# Revit family: vl-100s3_50Hz
name_source: partatom
category: 機械設備
units: mm (PartAtom-declared; Revit-internal decimal feet)

## family parameters
OmniClass タイトル = Centrifugal Fans
OmniClass 番号 = 23.75.35.17.27
パーツ タイプ = 標準
ロード時にボイドで切り取り = いいえ
丸型コネクタ寸法 = 直径を使用
作業面ベース = いいえ
共有 = いいえ
常に垂直 = はい
部屋計算ポイント = いいえ

## types (1)
- VL-100S3
    Clearance Back = 0  [stored 0 ft]
    Clearance Bottom = 100  [stored 0.328084 ft]
    Clearance Front = 500  [stored 1.64042 ft]
    Clearance Left = 50
    Clearance Right = 50
    Clearance Top = 120
    D1 = 206  [stored 0.675853 ft]
    Depth = 156  [stored 0.511811 ft]
    H1 = 289  [stored 0.948163 ft]
    H2 = 115  [stored 0.377297 ft]
    H3 = 137  [stored 0.449475 ft]
    Height = 235
    IfcExportAs = IfcFanType
    IfcExportType = CENTRIFUGALBACKWARDINCLINEDCURVED
    MAX静圧 = 0.0 Pa
    MAX風量 = 95.0 m³/h
    MID静圧 = 0.0 Pa
    MID風量 = 0.0 m³/h
    MIN静圧 = 0.0 Pa
    MIN風量 = 60.0 m³/h
    OmniClassCode = 23-33 31 19 13 13
    Pype_D = 150
    Pype_Depth = 100  [stored 0.328084 ft]
    URL = https://www.mitsubishielectric.co.jp
    Uniclass2015Code = Pr_65_67_29_89
    Uniclass2015Title = Twin centrifugal fans
    Uniclass2015Version = Systems v1.9
    W1 = 413  [stored 1.35499 ft]
    W2 = 200  [stored 0.656168 ft]
    W3 = 156  [stored 0.511811 ft]
    Width = 400  [stored 1.31234 ft]
    ダクト径 = 65 mm
    マテリアル = 合成樹脂(白)
    メンテナンススペース = はい
    モデル = VL-100S3
    仕様書バージョン = Version1.0
    企業コード = 108420
    価格 = 70000 $
    分類コード = 50052504100030
    周波数 = 50 Hz
    極数 = 2
    法定耐用年数 = 15
    消費電力 = 31 W
    温度交換効率 = 70.00%
    相 = 1
    積算_科目 = 2 換気設備
    製品リリース年月 = 2019年5月16日
    製品出荷対象 = 国内
    製品質量 = 6.70 kg
    製造元 = 三菱電機株式会社
    設置方法 = 壁付
    説明 = 換気空清機ロスナイ 本体セパレート取付タイプ
    負荷分類 = 3_ファン類
    質量 = 8.04 kg
    運転質量 = 0.00 kg
    電動機出力 = 0 W
    電圧 = 100 V

note: [stored X ft] marks values corroborated as IEEE doubles in the binary element streams (Revit-internal decimal feet)
